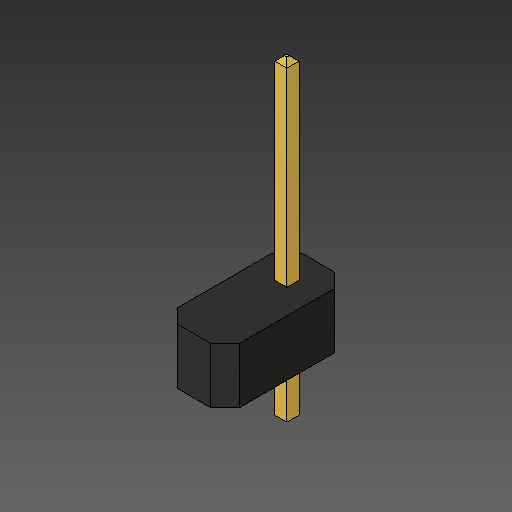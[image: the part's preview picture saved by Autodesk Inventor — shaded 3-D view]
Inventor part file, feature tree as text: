
AUTODESK INVENTOR PART (.ipt)
format: ipt  version: 2018.2 (Build 222227000, 227)  size: 93,696 bytes
history: native  units: mm
features: other x1, chamfer x1
ambient origin geometry x8: Origin, YZ Plane, XZ Plane, XY Plane, X Axis, Y Axis, Z Axis, Center Point
bodies: Body1 (feature_tree)
feature tree (2):
  other  "ソリッド1"
  chamfer  "Chamfer2"  [1 undecoded]
note: 1 required parameter value undecoded (feature->parameter linkage not recoverable at this tier; creation-order binding heuristic only, values carry confidence <= 0.55)
